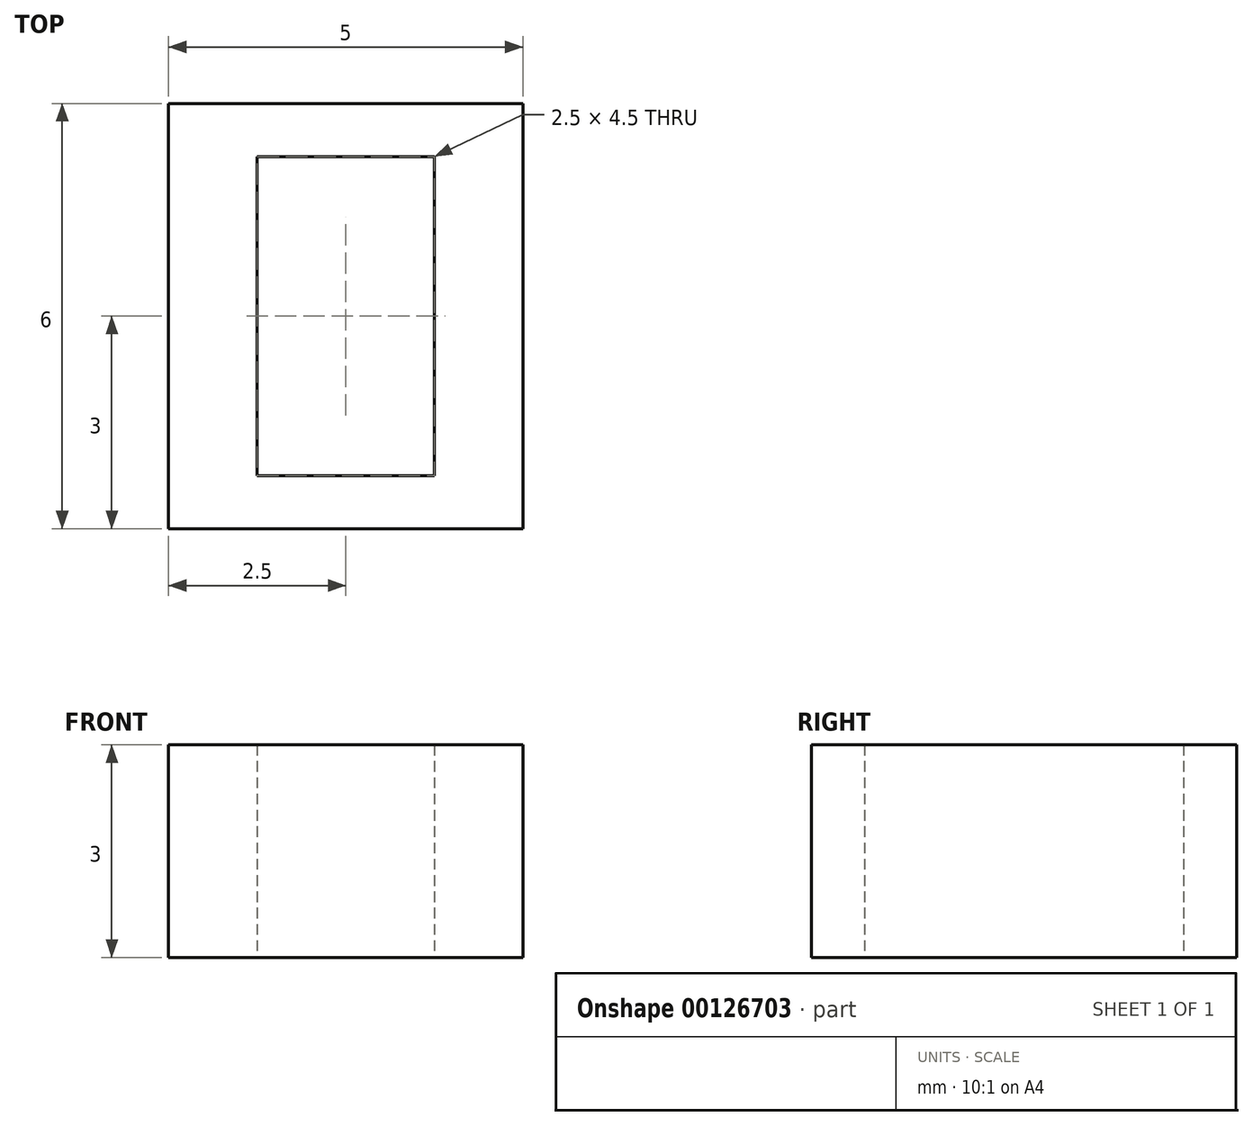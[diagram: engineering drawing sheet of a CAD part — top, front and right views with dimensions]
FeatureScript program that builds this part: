
annotation { "Feature Type Name" : "Feature", "Feature Type Description" : "" }
export const myFeature = defineFeature(function(context is Context, id is Id, definition is map)
    precondition{}
    {
        {
            var Q0;
            Q0=qCreatedBy(makeId("Top.planeOp"),FACE);
            var sketch = newSketch(context, id + "F0", { "sketchPlane" : qUnion([Q0])});
            skLineSegment(sketch, "E0.bottom", {"start": v(-1.25, 2.25) * mm, "end": v(1.25, 2.25) * mm});
            skLineSegment(sketch, "E0.top", {"start": v(-1.25, -2.25) * mm, "end": v(1.25, -2.25) * mm});
            skLineSegment(sketch, "E0.left", {"start": v(-1.25, 2.25) * mm, "end": v(-1.25, -2.25) * mm});
            skLineSegment(sketch, "E0.right", {"start": v(1.25, 2.25) * mm, "end": v(1.25, -2.25) * mm});
            skPoint(sketch, "E0.middle", {"position": v(0, 0) * mm});
            skLineSegment(sketch, "E1.bottom", {"start": v(-2.5, 3) * mm, "end": v(2.5, 3) * mm});
            skLineSegment(sketch, "E1.top", {"start": v(-2.5, -3) * mm, "end": v(2.5, -3) * mm});
            skLineSegment(sketch, "E1.left", {"start": v(-2.5, 3) * mm, "end": v(-2.5, -3) * mm});
            skLineSegment(sketch, "E1.right", {"start": v(2.5, 3) * mm, "end": v(2.5, -3) * mm});
            skSolve(sketch);
        }
        {
            var Q0;
            Q0=qSketchRegion(id+"F0",true);
            var Q1;
            Q1=makeQuery(id+"F0.imprint","IMPRINT",FACE,{"disambiguationData":[TD([[makeQuery(id+"F0.imprint","IMPRINT",EDGE,{"derivedFrom":sQuery(id+"F0.wireOp",EDGE,"E0.bottom")}),1.0]])]});
            extrude(context, id + "F1", {"entities" : qUnion([Q0, Q1]), "depth" : 3 * mm});
        }
    });
